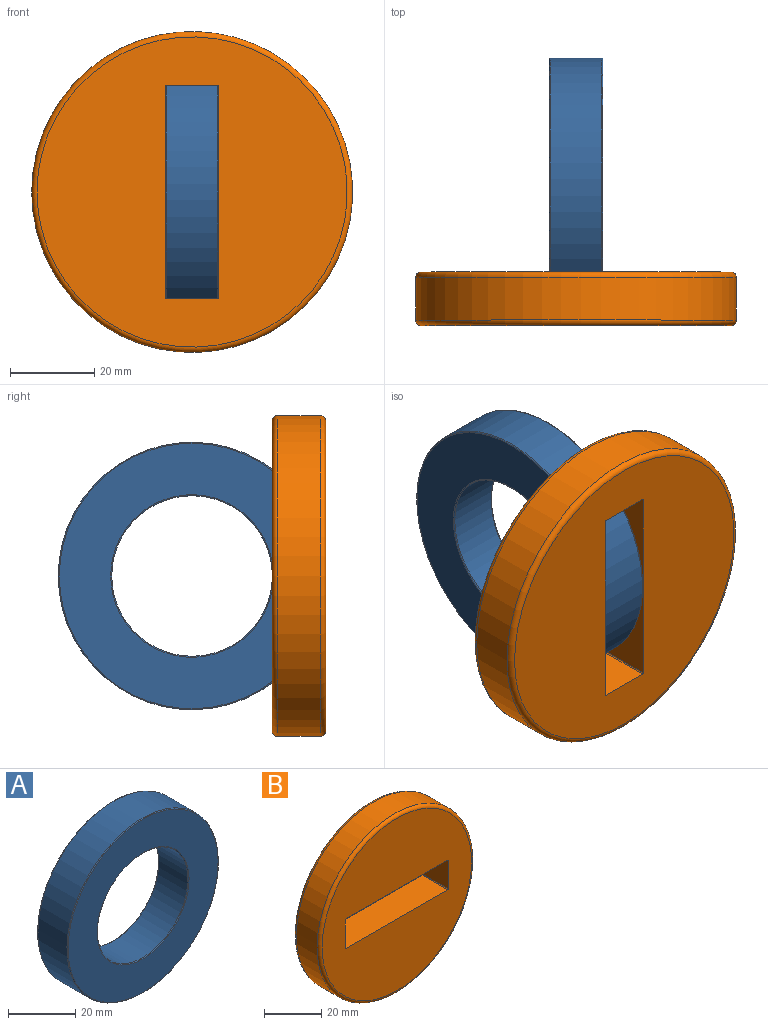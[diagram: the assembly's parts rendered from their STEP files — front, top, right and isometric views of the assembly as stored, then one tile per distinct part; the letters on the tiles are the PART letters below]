
ASSEMBLY  parts=2 mates=1
PART A: 8 faces, bbox 68.7x12.7x68.7 mm
  f0: cylinder r=19.05mm len=38.1mm, axis (0,1,0), area 1459.3mm2, adj f4,f6
  f1: cylinder r=31.75mm len=63.5mm, axis (0,1,0), area 2432.2mm2, adj f5,f7
  f2: plane 62.99x62.99mm, normal (0,-1,0), area 1945.8mm2, adj f6,f7
  f3: plane 62.99x62.99mm, normal (0,1,0), area 1945.8mm2, adj f4,f5
  f4: torus R=19.3mm, axis (0,-1,0), area 48mm2, adj f0,f3
  f5: torus R=31.5mm, axis (0,-1,0), area 79.4mm2, adj f1,f3
  f6: torus R=19.3mm, axis (0,-1,0), area 48mm2, adj f0,f2
  f7: torus R=31.5mm, axis (0,-1,0), area 79.4mm2, adj f1,f2
PART B: 13 faces, bbox 82.5x12.7x82.5 mm
  f0: plane 50.29x12.7mm, normal (0,0,1), area 638.7mm2, adj f1,f7,f9,f10
  f1: cylinder r=0.25mm len=12.7mm, axis (0,1,0), area 5.1mm2, adj f0,f2,f9,f10
  f2: plane 12.7x12.19mm, normal (1,0,0), area 154.8mm2, adj f1,f3,f9,f10
  f3: cylinder r=0.25mm len=12.7mm, axis (0,1,0), area 5.1mm2, adj f2,f4,f9,f10
  f4: plane 50.29x12.7mm, normal (0,0,-1), area 638.7mm2, adj f3,f5,f9,f10
  f5: cylinder r=0.25mm len=12.7mm, axis (0,1,0), area 5.1mm2, adj f4,f6,f9,f10
  f6: plane 12.7x12.19mm, normal (-1,0,0), area 154.8mm2, adj f5,f7,f9,f10
  f7: cylinder r=0.25mm len=12.7mm, axis (0,1,0), area 5.1mm2, adj f0,f6,f9,f10
  f8: cylinder r=38.1mm len=76.2mm, axis (0,1,0), area 2432.2mm2, adj f11,f12
  f9: plane 73.66x73.66mm, normal (0,-1,0), area 3616.3mm2, adj f0,f1,f2,f3,f4,f5,f6,f7
  f10: plane 73.66x73.66mm, normal (0,1,0), area 3616.3mm2, adj f0,f1,f2,f3,f4,f5,f6,f7
  f11: torus R=36.83mm, axis (0,-1,0), area 471.8mm2, adj f8,f10
  f12: torus R=36.83mm, axis (0,-1,0), area 471.8mm2, adj f8,f9
PLACE A rot(axis=(0.58,-0.58,0.58),120deg) t=(-121.82,14.43,4.16)mm
PLACE B rot(axis=(-0.71,0,-0.71),180deg) t=(-115.47,-17.32,4.16)mm
MATE fastened B.f4 <-> A.f2  axis (-1,0,0) through (-109.12,-10.97,4.16)mm
